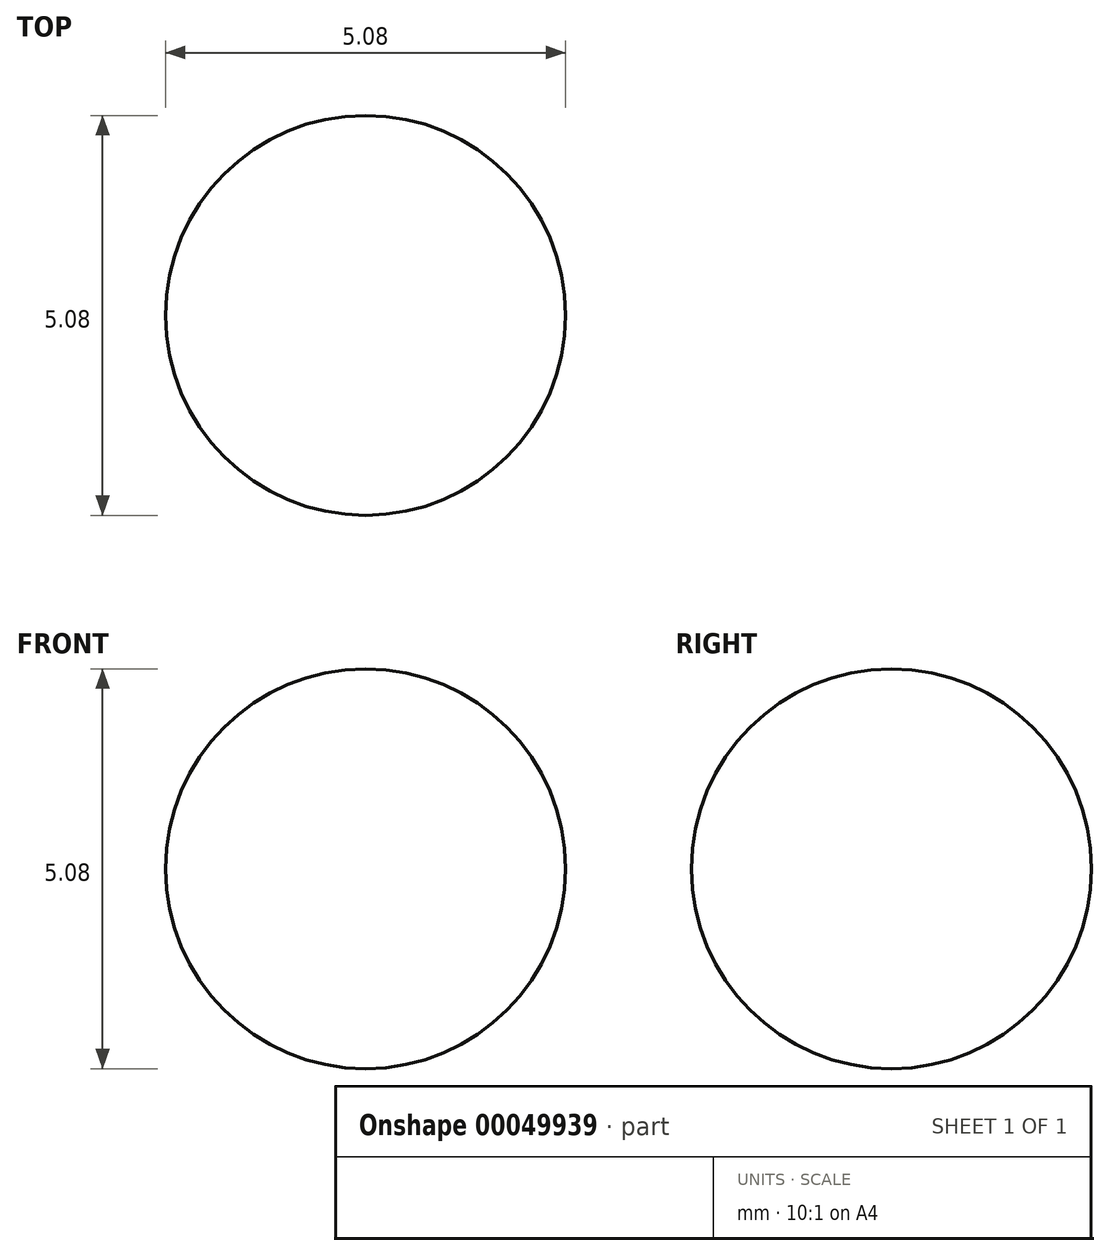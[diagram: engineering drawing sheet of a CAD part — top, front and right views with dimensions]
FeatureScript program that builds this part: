
annotation { "Feature Type Name" : "Feature", "Feature Type Description" : "" }
export const myFeature = defineFeature(function(context is Context, id is Id, definition is map)
    precondition{}
    {
        {
            var Q0;
            Q0=qCreatedBy(makeId("Front.planeOp"),FACE);
            var sketch = newSketch(context, id + "F0", { "sketchPlane" : qUnion([Q0])});
            skCircle(sketch, "E0", {"center": v(0, 0) * mm, "radius": 2.54 * mm});
            skLineSegment(sketch, "E1", {"start": v(0, 0) * mm, "end": v(2.54, 0) * mm});
            skSolve(sketch);
        }
        {
            var Q0;
            Q0 = qSketchRegion(id + "F0", true);
            extrude(context, id + "F1", {"entities" : qUnion([Q0]), "depth" : 5.08 * mm});
        }
        {
            var Q0;
            Q0=makeQuery(id+"F1.opExtrude","CAP_EDGE",EDGE,{"disambiguationData":[OSD([sQuery(id+"F0.wireOp",EDGE,"E0")])],"isStart":false});
            var Q1;
            Q1=makeQuery(id+"F1.opExtrude","CAP_FACE",FACE,{"disambiguationData":[OSD([sQuery(id+"F0.wireOp",EDGE,"E0")])],"isStart":false});
            fillet(context, id + "F2", {"entities" : qUnion([Q0, Q1]), "radius" : 2.54 * mm, "tangentPropagation" : true, "allowEdgeOverflow" : false});
        }
        {
            var Q0;
            Q0=makeQuery(id+"F1.opExtrude","CAP_FACE",FACE,{"disambiguationData":[OSD([sQuery(id+"F0.wireOp",EDGE,"E0")])],"isStart":true});
            fillet(context, id + "F3", {"entities" : qUnion([Q0]), "radius" : 2.54 * mm, "tangentPropagation" : true, "allowEdgeOverflow" : false});
        }
    });
